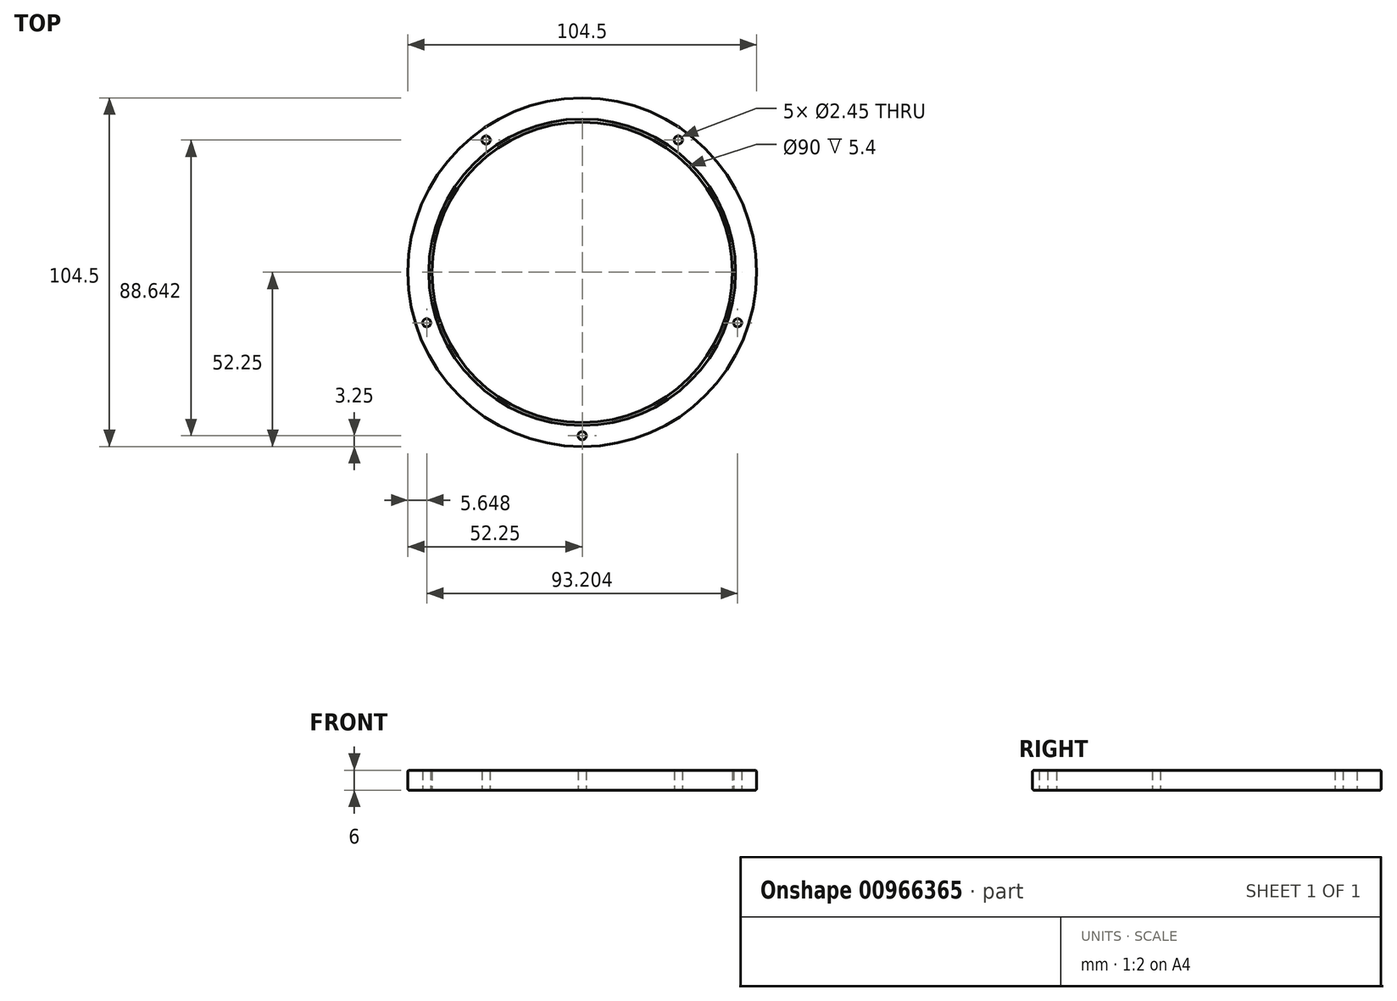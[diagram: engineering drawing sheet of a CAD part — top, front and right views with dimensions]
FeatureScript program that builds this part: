
annotation { "Feature Type Name" : "Feature", "Feature Type Description" : "" }
export const myFeature = defineFeature(function(context is Context, id is Id, definition is map)
    precondition{}
    {
        {
            var Q0;
            Q0=qCreatedBy(makeId("Top.planeOp"),FACE);
            var sketch = newSketch(context, id + "F0", { "sketchPlane" : qUnion([Q0])});
            skCircle(sketch, "E0", {"center": v(0, 0) * mm, "radius": 45 * mm});
            skCircle(sketch, "E1", {"center": v(0, 0) * mm, "radius": 52.25 * mm});
            skPoint(sketch, "E2", {"position": v(0, -49) * mm});
            skPoint(sketch, "E3.1.0", {"position": v(46.6, -15.14) * mm});
            skPoint(sketch, "E3.2.0", {"position": v(28.8, 39.64) * mm});
            skPoint(sketch, "E3.3.0", {"position": v(-28.8, 39.64) * mm});
            skPoint(sketch, "E3.4.0", {"position": v(-46.6, -15.14) * mm});
            skCircle(sketch, "E4", {"center": v(0, -49) * mm, "radius": 1.23 * mm});
            skCircle(sketch, "E5", {"center": v(46.6, -15.14) * mm, "radius": 1.23 * mm});
            skCircle(sketch, "E6", {"center": v(28.8, 39.64) * mm, "radius": 1.23 * mm});
            skCircle(sketch, "E7", {"center": v(-28.8, 39.64) * mm, "radius": 1.23 * mm});
            skCircle(sketch, "E8", {"center": v(-46.6, -15.14) * mm, "radius": 1.23 * mm});
            skSolve(sketch);
        }
        {
            var Q0;
            Q0=qSketchRegion(id+"F0",true);
            extrude(context, id + "F1", {"entities" : qUnion([Q0]), "depth" : 6 * mm, "offsetDistance" : 25 * mm});
        }
        {
            var Q0;
            Q0=makeQuery(id+"F1.opExtrude","CAP_EDGE",EDGE,{"disambiguationData":[OSD([sQuery(id+"F0.wireOp",EDGE,"E0")])],"isStart":false});
            fillet(context, id + "F2", {"entities" : qUnion([Q0]), "radius" : 1.5 * mm, "tangentPropagation" : true, "allowEdgeOverflow" : false});
        }
        {
            var Q0;
            Q0=qSketchRegion(id+"F0",true);
            extrude(context, id + "F3", {"entities" : qUnion([Q0]), "operationType" : NewBodyOperationType.ADD, "depth" : 5.9 * mm, "offsetDistance" : 25 * mm});
        }
        {
            var Q0;
            Q0=makeQuery(id+"F1.opExtrude","CAP_EDGE",EDGE,{"disambiguationData":[OSD([sQuery(id+"F0.wireOp",EDGE,"E0")])],"isStart":true});
            var Q1;
            Q1=makeQuery(id+"F1.opExtrude","CAP_EDGE",EDGE,{"disambiguationData":[OSD([sQuery(id+"F0.wireOp",EDGE,"E1")])],"isStart":true});
            var Q2;
            Q2=makeQuery(id+"F1.opExtrude","CAP_EDGE",EDGE,{"disambiguationData":[OSD([sQuery(id+"F0.wireOp",EDGE,"E1")])],"isStart":false});
            fillet(context, id + "F4", {"entities" : qUnion([Q0, Q1, Q2]), "radius" : .5 * mm, "tangentPropagation" : true, "allowEdgeOverflow" : false});
        }
    });
